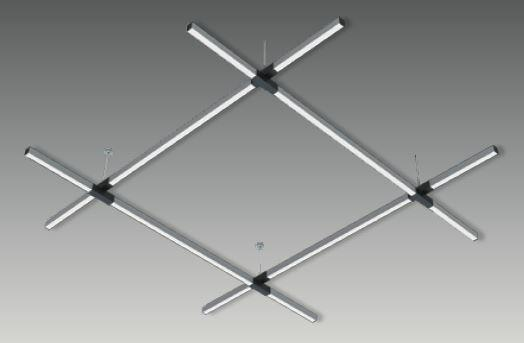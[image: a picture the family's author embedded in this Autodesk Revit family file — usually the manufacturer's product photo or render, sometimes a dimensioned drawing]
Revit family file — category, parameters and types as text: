
# Revit family: S 3030 PLG
name_source: partatom
category: Lighting Fixtures
revit_build: Autodesk Revit 2017 (Build: 20160225_1515(x64)
units: mm (PartAtom-declared; Revit-internal decimal feet)

## family parameters
Cut with Voids When Loaded = No
Host = Face
Light Source = Yes
Part Type = Normal
Room Calculation Point = No
Round Connector Dimension = Use Diameter
Shared = No

## types (2) — shared parameters
Color Filter = 16777215
Default Elevation = 1219 mm
Dimming Lamp Color Temperature Shift = <None>
Emit Shape Visible in Rendering = Yes
Emit from Rectangle Length = 1400 mm  [stored 4.59318 ft]
Emit from Rectangle Width = 40 mm  [stored 0.131234 ft]
Light Source Symbol Size = 610 mm
Manufacturer = ARLIGHT
Type Image = S 3030 PLG.JPG
Wattage Comments = 436W

## type names (no varying parameters)
- SPLG.3030.436.30
- SPLG.3030.436.40

note: [stored X ft] marks values corroborated as IEEE doubles in the binary element streams (Revit-internal decimal feet)

## geometry (parser evidence)
native form markers: Sweep x8
no freeform markers — native parametric forms only
